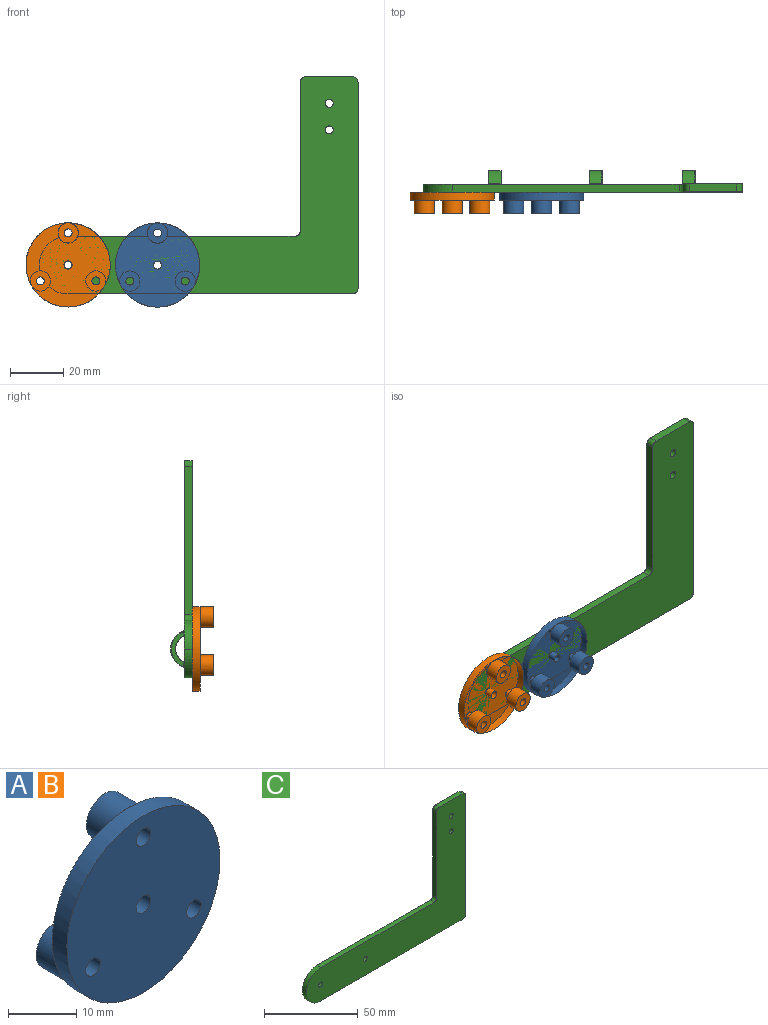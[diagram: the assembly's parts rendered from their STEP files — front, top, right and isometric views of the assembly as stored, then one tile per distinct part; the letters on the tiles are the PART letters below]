
ASSEMBLY  parts=3 mates=2
PART A: 13 faces, bbox 31.7x8x31.7 mm
  f0: cylinder r=1.5mm len=3mm, axis (0,-1,0), area 28.3mm2, adj f2,f3
  f1: cylinder r=15.85mm len=31.7mm, axis (0,-1,0), area 298.8mm2, adj f2,f3
  f2: plane 31.7x31.7mm, normal (0,1,0), area 646.1mm2, adj f0,f1,f4,f6,f8
  f3: plane 31.7x31.7mm, normal (0,-1,0), area 761mm2, adj f0,f1,f10,f11,f12
  f4: cylinder r=3.8mm len=7.6mm, axis (0,-1,0), area 119.4mm2, adj f2,f5
  f5: plane 7.6x7.6mm, normal (0,1,0), area 38.3mm2, adj f4,f12
  f6: cylinder r=3.8mm len=7.6mm, axis (0,-1,0), area 119.4mm2, adj f2,f7
  f7: plane 7.6x7.6mm, normal (0,1,0), area 38.3mm2, adj f6,f11
  f8: cylinder r=3.8mm len=7.6mm, axis (0,-1,0), area 119.4mm2, adj f2,f9
  f9: plane 7.6x7.6mm, normal (0,1,0), area 38.3mm2, adj f8,f10
  f10: cylinder r=1.5mm len=8mm, axis (0,1,0), area 75.4mm2, adj f3,f9
  f11: cylinder r=1.5mm len=8mm, axis (0,1,0), area 75.4mm2, adj f3,f7
  f12: cylinder r=1.5mm len=8mm, axis (0,1,0), area 75.4mm2, adj f3,f5
PART B: same geometry as A
PART C: 89 faces, bbox 120x8.7x81.7 mm
  f0: plane 120x81.7mm, normal (0,1,0), area 3742.3mm2, adj f1,f2,f3,f4,f5,f6,f7,f9
  f1: plane 77.7x3mm, normal (1,0,0), area 233.1mm2, adj f0,f8,f14,f15
  f2: plane 17.7x3mm, normal (0,0,1), area 53.1mm2, adj f0,f8,f15,f16
  f3: plane 56x3mm, normal (-1,0,0), area 168mm2, adj f0,f8,f13,f16
  f4: plane 85.4x3mm, normal (0,0,1), area 256.2mm2, adj f0,f8,f12,f13
  f5: cylinder r=1.5mm len=3mm, axis (0,-1,0), area 28.3mm2, adj f0,f8
  f6: plane 107.1x3mm, normal (0,0,-1), area 321.3mm2, adj f0,f8,f11,f14
  f7: cylinder r=1.5mm len=3mm, axis (0,-1,0), area 28.3mm2, adj f0,f8
  f8: plane 120x81.7mm, normal (0,-1,0), area 3825mm2, adj f1,f2,f3,f4,f5,f6,f7,f9
  f9: cylinder r=1.5mm len=3mm, axis (0,-1,0), area 28.3mm2, adj f0,f8
  f10: cylinder r=1.5mm len=3mm, axis (0,-1,0), area 28.3mm2, adj f0,f8
  f11: cylinder r=10.9mm len=10.9mm, axis (0,1,0), area 51.2mm2, adj f0,f6,f8,f12
  f12: cylinder r=10.9mm len=10.9mm, axis (0,-1,0), area 51.2mm2, adj f0,f4,f8,f11
  f13: cylinder r=2mm len=3mm, axis (0,-1,0), area 9.4mm2, adj f0,f3,f4,f8
  f14: cylinder r=2mm len=3mm, axis (0,-1,0), area 9.4mm2, adj f0,f1,f6,f8
  f15: cylinder r=2mm len=3mm, axis (0,1,0), area 9.4mm2, adj f0,f1,f2,f8
  f16: cylinder r=2mm len=3mm, axis (0,1,0), area 9.4mm2, adj f0,f2,f3,f8
  f17: cylinder r=5.14mm len=9.2mm, axis (-1,0,0), area 52.4mm2, adj f77,f82,f85,f88
  f18: cylinder r=7.14mm len=13.62mm, axis (-1,0,0), area 83.1mm2, adj f69,f73,f74,f75
  f19: plane 13.16x4.74mm, normal (1,0,0), area 23.6mm2, adj f72,f73,f82,f83
  f20: plane 13.16x4.74mm, normal (-1,0,0), area 23.6mm2, adj f75,f76,f84,f85
  f21: cylinder r=5.14mm len=9.2mm, axis (-1,0,0), area 52.4mm2, adj f57,f62,f65,f68
  f22: cylinder r=7.14mm len=13.62mm, axis (-1,0,0), area 83.1mm2, adj f49,f53,f54,f55
  f23: plane 13.16x4.74mm, normal (1,0,0), area 23.6mm2, adj f52,f53,f62,f63
  f24: plane 13.16x4.74mm, normal (-1,0,0), area 23.6mm2, adj f55,f56,f64,f65
  f25: cylinder r=5.14mm len=9.2mm, axis (-1,0,0), area 52.4mm2, adj f37,f42,f45,f48
  f26: cylinder r=7.14mm len=13.62mm, axis (-1,0,0), area 83.1mm2, adj f29,f33,f34,f35
  f27: plane 13.16x4.74mm, normal (1,0,0), area 23.6mm2, adj f32,f33,f42,f43
  f28: plane 13.16x4.74mm, normal (-1,0,0), area 23.6mm2, adj f35,f36,f44,f45
  f29: cylinder r=0.2mm len=4.6mm, axis (-1,0,0), area 1.2mm2, adj f0,f26,f30,f31
  f30: bspline ~0.52x0.48mm, area 0.1mm2, adj f0,f29,f32,f33
  f31: bspline ~0.49x0.48mm, area 0.1mm2, adj f0,f29,f35,f36
  f32: cylinder r=0.2mm len=1.72mm, axis (0,0,1), area 0.5mm2, adj f0,f27,f30,f38
  f33: torus R=6.94mm, axis (1,0,0), area 5.6mm2, adj f26,f27,f30,f39
  f34: cylinder r=0.2mm len=4.6mm, axis (-1,0,0), area 1.2mm2, adj f0,f26,f39,f40
  f35: torus R=6.94mm, axis (1,0,0), area 5.6mm2, adj f26,f28,f31,f40
  f36: cylinder r=0.2mm len=1.72mm, axis (0,0,-1), area 0.5mm2, adj f0,f28,f31,f41
  f37: cylinder r=0.2mm len=4.6mm, axis (-1,0,0), area 1.9mm2, adj f0,f25,f38,f41
  f38: bspline ~0.49x0.48mm, area 0.2mm2, adj f0,f32,f37,f42
  f39: bspline ~0.49x0.48mm, area 0.1mm2, adj f0,f33,f34,f43
  f40: bspline ~0.52x0.48mm, area 0.1mm2, adj f0,f34,f35,f44
  f41: bspline ~0.55x0.44mm, area 0.2mm2, adj f0,f36,f37,f45
  f42: torus R=5.34mm, axis (1,0,0), area 3.7mm2, adj f25,f27,f38,f46
  f43: cylinder r=0.2mm len=1.72mm, axis (0,0,1), area 0.5mm2, adj f0,f27,f39,f46
  f44: cylinder r=0.2mm len=1.72mm, axis (0,0,-1), area 0.5mm2, adj f0,f28,f40,f47
  f45: torus R=5.34mm, axis (1,0,0), area 3.7mm2, adj f25,f28,f41,f47
  f46: bspline ~0.55x0.44mm, area 0.2mm2, adj f0,f42,f43,f48
  f47: bspline ~0.49x0.48mm, area 0.2mm2, adj f0,f44,f45,f48
  f48: cylinder r=0.2mm len=4.6mm, axis (-1,0,0), area 1.9mm2, adj f0,f25,f46,f47
  f49: cylinder r=0.2mm len=4.6mm, axis (-1,0,0), area 1.2mm2, adj f0,f22,f50,f51
  f50: bspline ~0.52x0.48mm, area 0.1mm2, adj f0,f49,f52,f53
  f51: bspline ~0.49x0.48mm, area 0.1mm2, adj f0,f49,f55,f56
  f52: cylinder r=0.2mm len=1.72mm, axis (0,0,1), area 0.5mm2, adj f0,f23,f50,f58
  f53: torus R=6.94mm, axis (1,0,0), area 5.6mm2, adj f22,f23,f50,f59
  f54: cylinder r=0.2mm len=4.6mm, axis (-1,0,0), area 1.2mm2, adj f0,f22,f59,f60
  f55: torus R=6.94mm, axis (1,0,0), area 5.6mm2, adj f22,f24,f51,f60
  f56: cylinder r=0.2mm len=1.72mm, axis (0,0,-1), area 0.5mm2, adj f0,f24,f51,f61
  f57: cylinder r=0.2mm len=4.6mm, axis (-1,0,0), area 1.9mm2, adj f0,f21,f58,f61
  f58: bspline ~0.49x0.48mm, area 0.2mm2, adj f0,f52,f57,f62
  f59: bspline ~0.49x0.48mm, area 0.1mm2, adj f0,f53,f54,f63
  f60: bspline ~0.52x0.48mm, area 0.1mm2, adj f0,f54,f55,f64
  f61: bspline ~0.55x0.44mm, area 0.2mm2, adj f0,f56,f57,f65
  f62: torus R=5.34mm, axis (1,0,0), area 3.7mm2, adj f21,f23,f58,f66
  f63: cylinder r=0.2mm len=1.72mm, axis (0,0,1), area 0.5mm2, adj f0,f23,f59,f66
  f64: cylinder r=0.2mm len=1.72mm, axis (0,0,-1), area 0.5mm2, adj f0,f24,f60,f67
  f65: torus R=5.34mm, axis (1,0,0), area 3.7mm2, adj f21,f24,f61,f67
  f66: bspline ~0.55x0.44mm, area 0.2mm2, adj f0,f62,f63,f68
  f67: bspline ~0.49x0.48mm, area 0.2mm2, adj f0,f64,f65,f68
  f68: cylinder r=0.2mm len=4.6mm, axis (-1,0,0), area 1.9mm2, adj f0,f21,f66,f67
  f69: cylinder r=0.2mm len=4.6mm, axis (-1,0,0), area 1.2mm2, adj f0,f18,f70,f71
  f70: bspline ~0.52x0.48mm, area 0.1mm2, adj f0,f69,f72,f73
  f71: bspline ~0.49x0.48mm, area 0.1mm2, adj f0,f69,f75,f76
  f72: cylinder r=0.2mm len=1.72mm, axis (0,0,-1), area 0.5mm2, adj f0,f19,f70,f78
  f73: torus R=6.94mm, axis (1,0,0), area 5.6mm2, adj f18,f19,f70,f79
  f74: cylinder r=0.2mm len=4.6mm, axis (-1,0,0), area 1.2mm2, adj f0,f18,f79,f80
  f75: torus R=6.94mm, axis (1,0,0), area 5.6mm2, adj f18,f20,f71,f80
  f76: cylinder r=0.2mm len=1.72mm, axis (0,0,1), area 0.5mm2, adj f0,f20,f71,f81
  f77: cylinder r=0.2mm len=4.6mm, axis (-1,0,0), area 1.9mm2, adj f0,f17,f78,f81
  f78: bspline ~0.49x0.48mm, area 0.2mm2, adj f0,f72,f77,f82
  f79: bspline ~0.49x0.48mm, area 0.1mm2, adj f0,f73,f74,f83
  f80: bspline ~0.52x0.48mm, area 0.1mm2, adj f0,f74,f75,f84
  f81: bspline ~0.55x0.44mm, area 0.2mm2, adj f0,f76,f77,f85
  f82: torus R=5.34mm, axis (1,0,0), area 3.7mm2, adj f17,f19,f78,f86
  f83: cylinder r=0.2mm len=1.72mm, axis (0,0,-1), area 0.5mm2, adj f0,f19,f79,f86
  f84: cylinder r=0.2mm len=1.72mm, axis (0,0,1), area 0.5mm2, adj f0,f20,f80,f87
  f85: torus R=5.34mm, axis (1,0,0), area 3.7mm2, adj f17,f20,f81,f87
  f86: bspline ~0.55x0.44mm, area 0.2mm2, adj f0,f82,f83,f88
  f87: bspline ~0.49x0.48mm, area 0.2mm2, adj f0,f84,f85,f88
  f88: cylinder r=0.2mm len=4.6mm, axis (-1,0,0), area 1.9mm2, adj f0,f17,f86,f87
PLACE A rot(axis=(0,0,1),180deg) t=(23.97,58.57,0.16)mm
PLACE B rot(axis=(0,0,1),180deg) t=(-9.68,58.57,0.21)mm
PLACE C t=(39.42,58.57,0.16)mm
MATE fastened B.f0 <-> C.f11  axis (0,1,0) through (-9.68,58.57,0.21)mm
MATE fastened A.f0 <-> C.f9  axis (0,1,0) through (23.97,58.57,0.16)mm
